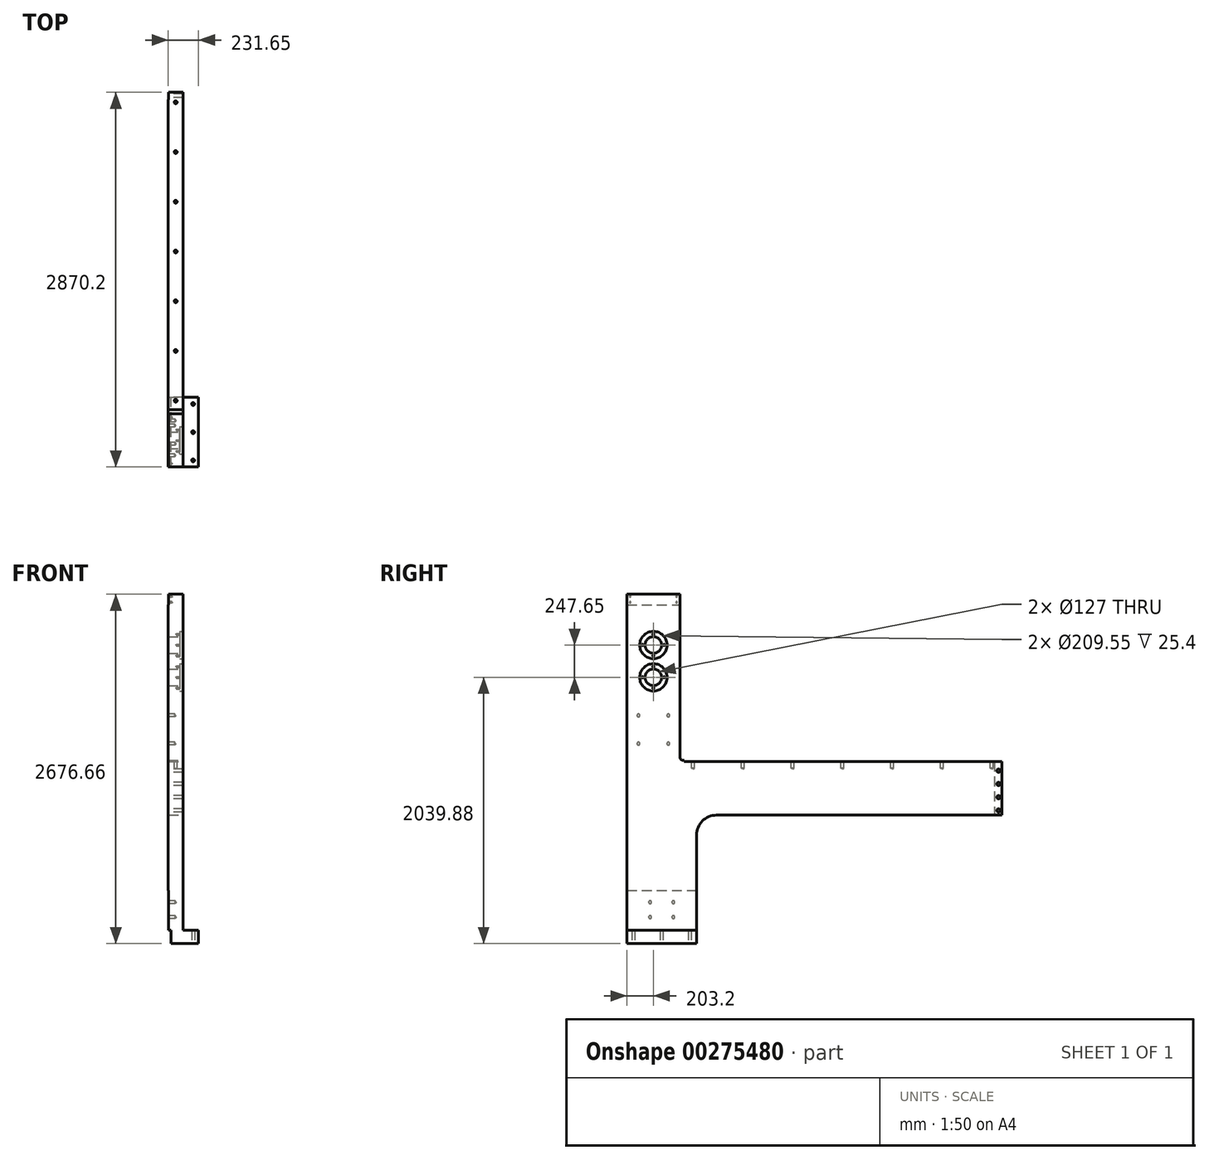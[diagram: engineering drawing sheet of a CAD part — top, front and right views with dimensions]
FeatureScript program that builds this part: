
annotation { "Feature Type Name" : "Feature", "Feature Type Description" : "" }
export const myFeature = defineFeature(function(context is Context, id is Id, definition is map)
    precondition{}
    {
        {
            var Q0;
            Q0=qCreatedBy(makeId("Right.planeOp"),FACE);
            var sketch = newSketch(context, id + "F0", { "sketchPlane" : qUnion([Q0])});
            skLineSegment(sketch, "E0", {"start": v(0, 1338.33) * mm, "end": v(0, -1338.33) * mm});
            skLineSegment(sketch, "E1.bottom", {"start": v(0, 1338.33) * mm, "end": v(406.4, 1338.33) * mm});
            skLineSegment(sketch, "E1.left", {"start": v(0, 1338.33) * mm, "end": v(0, -642.77) * mm});
            skLineSegment(sketch, "E1.right", {"start": v(406.4, 1338.33) * mm, "end": v(406.4, 90.42) * mm});
            skLineSegment(sketch, "E2", {"start": v(0, -1338.33) * mm, "end": v(2674.85, -1338.33) * mm, "construction": true});
            skLineSegment(sketch, "E3.0", {"start": v(0, -1236.73) * mm, "end": v(897.1, -1236.73) * mm, "construction": true});
            skLineSegment(sketch, "E4.bottom", {"start": v(0, -1236.73) * mm, "end": v(533.4, -1236.73) * mm});
            skLineSegment(sketch, "E4.top", {"start": v(406.4, 65.02) * mm, "end": v(438.15, 65.02) * mm});
            skLineSegment(sketch, "E4.left", {"start": v(0, -1236.73) * mm, "end": v(0, 65.02) * mm});
            skLineSegment(sketch, "E4.right", {"start": v(533.4, -1236.73) * mm, "end": v(533.4, -506.48) * mm});
            skLineSegment(sketch, "E5.bottom", {"start": v(431.8, 65.02) * mm, "end": v(438.15, 65.02) * mm});
            skLineSegment(sketch, "E5.top", {"start": v(685.8, -354.08) * mm, "end": v(2870.2, -354.08) * mm});
            skLineSegment(sketch, "E5.left", {"start": v(0, 65.02) * mm, "end": v(0, -354.08) * mm});
            skLineSegment(sketch, "E5.right", {"start": v(2870.2, 57.02) * mm, "end": v(2870.2, -354.08) * mm});
            skPoint(sketch, "E6.visualSharp", {"position": v(533.4, -354.08) * mm});
            skArc(sketch, "E6.filletArc", {"start": v(685.8, -354.08) * mm, "mid": v(578.04, -398.71) * mm, "end": v(533.4, -506.48) * mm});
            skPoint(sketch, "E7.visualSharp", {"position": v(406.4, 65.02) * mm});
            skArc(sketch, "E7.filletArc", {"start": v(406.4, 90.42) * mm, "mid": v(413.84, 72.46) * mm, "end": v(431.8, 65.02) * mm});
            skLineSegment(sketch, "E8.0", {"start": v(0, 701.55) * mm, "end": v(2674.85, 701.55) * mm, "construction": true});
            skLineSegment(sketch, "E9.0", {"start": v(0, 949.2) * mm, "end": v(2674.85, 949.2) * mm, "construction": true});
            skLineSegment(sketch, "E10", {"start": v(203.2, 1338.33) * mm, "end": v(203.2, -548.87) * mm, "construction": true});
            skCircle(sketch, "E11", {"center": v(203.2, 949.2) * mm, "radius": 63.5 * mm});
            skCircle(sketch, "E12", {"center": v(203.2, 701.55) * mm, "radius": 63.5 * mm});
            skLineSegment(sketch, "E13.0", {"start": v(438.15, 1338.33) * mm, "end": v(438.15, 701.55) * mm, "construction": true});
            skLineSegment(sketch, "E14.0", {"start": v(0, 57.02) * mm, "end": v(203.2, 57.02) * mm, "construction": true});
            skLineSegment(sketch, "E15.trimOffspring", {"start": v(438.15, 57.02) * mm, "end": v(2870.2, 57.02) * mm});
            skLineSegment(sketch, "E16.trimOffspring", {"start": v(438.15, 65.02) * mm, "end": v(438.15, 57.02) * mm});
            skSolve(sketch);
        }
        {
            var Q0;
            Q0=qSketchRegion(id+"F0",true);
            extrude(context, id + "F1", {"entities" : qUnion([Q0]), "endBound" : BoundingType.SYMMETRIC, "depth" : 114.3 * mm});
        }
        {
            var Q0;
            Q0=makeQuery(id+"F1.opExtrude","CAP_FACE",FACE,{"disambiguationData":[OSD([sQuery(id+"F0.wireOp",EDGE,"E1.bottom"),sQuery(id+"F0.wireOp",EDGE,"E1.left"),sQuery(id+"F0.wireOp",EDGE,"E1.right"),sQuery(id+"F0.wireOp",EDGE,"E4.bottom"),sQuery(id+"F0.wireOp",EDGE,"E4.left"),sQuery(id+"F0.wireOp",EDGE,"E4.right"),sQuery(id+"F0.wireOp",EDGE,"E5.bottom"),sQuery(id+"F0.wireOp",EDGE,"E5.top"),sQuery(id+"F0.wireOp",EDGE,"E5.left"),sQuery(id+"F0.wireOp",EDGE,"E5.right"),sQuery(id+"F0.wireOp",EDGE,"E6.filletArc"),sQuery(id+"F0.wireOp",EDGE,"E7.filletArc"),sQuery(id+"F0.wireOp",EDGE,"E11"),sQuery(id+"F0.wireOp",EDGE,"E12"),sQuery(id+"F0.wireOp",EDGE,"E15.trimOffspring"),sQuery(id+"F0.wireOp",EDGE,"E16.trimOffspring")])],"isStart":false});
            var sketch = newSketch(context, id + "F2", { "sketchPlane" : qUnion([Q0])});
            skLineSegment(sketch, "E17.bottom", {"start": v(0, 1338.33) * mm, "end": v(406.4, 1338.33) * mm});
            skLineSegment(sketch, "E17.top", {"start": v(0, 1255.78) * mm, "end": v(406.4, 1255.78) * mm});
            skLineSegment(sketch, "E17.left", {"start": v(0, 1338.33) * mm, "end": v(0, 1255.78) * mm});
            skLineSegment(sketch, "E17.right", {"start": v(406.4, 1338.33) * mm, "end": v(406.4, 1255.78) * mm});
            skSolve(sketch);
        }
        {
            var Q0;
            Q0=makeQuery(id+"F2.imprint","IMPRINT",FACE,{"disambiguationData":[TD([[makeQuery(id+"F2.imprint","IMPRINT",EDGE,{"derivedFrom":sQuery(id+"F2.wireOp",EDGE,"E17.bottom")}),-1.0]])]});
            extrude(context, id + "F3", {"entities" : qUnion([Q0]), "operationType" : NewBodyOperationType.REMOVE, "oppositeDirection" : true, "depth" : 3.05 * mm});
        }
        {
            var Q0;
            Q0=makeQuery(id+"F3.boolean.opBoolean","COPY",FACE,{"derivedFrom":makeQuery(id+"F3.opExtrude","CAP_FACE",FACE,{"disambiguationData":[OSD([sQuery(id+"F2.wireOp",EDGE,"E17.bottom"),sQuery(id+"F2.wireOp",EDGE,"E17.top"),sQuery(id+"F2.wireOp",EDGE,"E17.left"),sQuery(id+"F2.wireOp",EDGE,"E17.right")])],"isStart":false})});
            var sketch = newSketch(context, id + "F4", { "sketchPlane" : qUnion([Q0])});
            skLineSegment(sketch, "E18", {"start": v(203.2, 1338.33) * mm, "end": v(203.2, 1255.78) * mm, "construction": true});
            skCircle(sketch, "E19.0", {"center": v(203.2, 949.2) * mm, "radius": 63.5 * mm, "construction": true});
            skLineSegment(sketch, "E20", {"start": v(203.2, 949.2) * mm, "end": v(580.51, 949.2) * mm, "construction": true});
            skLineSegment(sketch, "E21.0", {"start": v(25.4, 1276.22) * mm, "end": v(580.51, 1276.22) * mm, "construction": true});
            skLineSegment(sketch, "E22.0", {"start": v(25.4, 1320.67) * mm, "end": v(580.51, 1320.67) * mm, "construction": true});
            skLineSegment(sketch, "E23.0", {"start": v(25.4, 1338.33) * mm, "end": v(25.4, 1255.78) * mm, "construction": true});
            skPoint(sketch, "E24", {"position": v(25.4, 1320.67) * mm});
            skPoint(sketch, "E25", {"position": v(25.4, 1276.22) * mm});
            skPoint(sketch, "E26.MirrorP", {"position": v(381, 1320.67) * mm});
            skPoint(sketch, "E27.MirrorP", {"position": v(381, 1276.22) * mm});
            skSolve(sketch);
        }
        {
            var Q0;
            Q0=sQuery(id+"F4.wireOp",VERTEX,"E24");
            var Q1;
            Q1=sQuery(id+"F4.wireOp",VERTEX,"E25");
            var Q2;
            Q2=sQuery(id+"F4.wireOp",VERTEX,"E26.MirrorP");
            var Q3;
            Q3=sQuery(id+"F4.wireOp",VERTEX,"E27.MirrorP");
            var Q4;
            Q4=makeQuery(id+"F1.opExtrude","SWEPT_BODY",BODY,{"disambiguationData":[OSD([sQuery(id+"F0.wireOp",EDGE,"E1.bottom"),sQuery(id+"F0.wireOp",EDGE,"E1.left"),sQuery(id+"F0.wireOp",EDGE,"E1.right"),sQuery(id+"F0.wireOp",EDGE,"E4.bottom"),sQuery(id+"F0.wireOp",EDGE,"E4.left"),sQuery(id+"F0.wireOp",EDGE,"E4.right"),sQuery(id+"F0.wireOp",EDGE,"E5.bottom"),sQuery(id+"F0.wireOp",EDGE,"E5.top"),sQuery(id+"F0.wireOp",EDGE,"E5.left"),sQuery(id+"F0.wireOp",EDGE,"E5.right"),sQuery(id+"F0.wireOp",EDGE,"E6.filletArc"),sQuery(id+"F0.wireOp",EDGE,"E7.filletArc"),sQuery(id+"F0.wireOp",EDGE,"E11"),sQuery(id+"F0.wireOp",EDGE,"E12"),sQuery(id+"F0.wireOp",EDGE,"E15.trimOffspring"),sQuery(id+"F0.wireOp",EDGE,"E16.trimOffspring")])]});
            hole(context, id + "F5", {"style" : HoleStyle.SIMPLE, "endStyle" : HoleEndStyle.BLIND, "standardTappedOrClearance" : lookupTablePath({ "standard" : "ANSI", "engagement" : "75%", "pitch" : "13 tpi", "size" : "1/2", "type" : "Tapped" }), "standardBlindInLast" : lookupTablePath({ "standard" : "ANSI", "engagement" : "75%", "pitch" : "13 tpi", "size" : "1/2", "type" : "Tapped" }), "holeDiameter" : 10.72 * mm, "showTappedDepth" : true, "holeDepth" : 25.4 * mm, "tappedDepth" : 19.54 * mm, "tapClearance" : 3, "startFromSketch" : true, "locations" : qUnion([Q0, Q1, Q2, Q3]), "scope" : qUnion([Q4]), "majorDiameter" : 12.7 * mm});
        }
        {
            var Q0;
            Q0=makeQuery(id+"F1.opExtrude","CAP_FACE",FACE,{"disambiguationData":[OSD([sQuery(id+"F0.wireOp",EDGE,"E1.bottom"),sQuery(id+"F0.wireOp",EDGE,"E1.left"),sQuery(id+"F0.wireOp",EDGE,"E1.right"),sQuery(id+"F0.wireOp",EDGE,"E4.bottom"),sQuery(id+"F0.wireOp",EDGE,"E4.left"),sQuery(id+"F0.wireOp",EDGE,"E4.right"),sQuery(id+"F0.wireOp",EDGE,"E5.bottom"),sQuery(id+"F0.wireOp",EDGE,"E5.top"),sQuery(id+"F0.wireOp",EDGE,"E5.left"),sQuery(id+"F0.wireOp",EDGE,"E5.right"),sQuery(id+"F0.wireOp",EDGE,"E6.filletArc"),sQuery(id+"F0.wireOp",EDGE,"E7.filletArc"),sQuery(id+"F0.wireOp",EDGE,"E11"),sQuery(id+"F0.wireOp",EDGE,"E12"),sQuery(id+"F0.wireOp",EDGE,"E15.trimOffspring"),sQuery(id+"F0.wireOp",EDGE,"E16.trimOffspring")])],"isStart":true});
            var sketch = newSketch(context, id + "F6", { "sketchPlane" : qUnion([Q0])});
            skCircle(sketch, "E28.0", {"center": v(-203.2, 949.2) * mm, "radius": 63.5 * mm, "construction": true});
            skCircle(sketch, "E29.0", {"center": v(-203.2, 701.55) * mm, "radius": 63.5 * mm, "construction": true});
            skCircle(sketch, "E30", {"center": v(-203.2, 949.2) * mm, "radius": 104.78 * mm});
            skCircle(sketch, "E31", {"center": v(-203.2, 701.55) * mm, "radius": 104.78 * mm});
            skSolve(sketch);
        }
        {
            var Q0;
            Q0=qSketchRegion(id+"F6",true);
            extrude(context, id + "F7", {"entities" : qUnion([Q0]), "operationType" : NewBodyOperationType.REMOVE, "oppositeDirection" : true, "depth" : 25.4 * mm});
        }
        {
            var Q0;
            Q0=makeQuery(id+"F7.boolean.opBoolean","COPY",FACE,{"derivedFrom":makeQuery(id+"F7.opExtrude","CAP_FACE",FACE,{"disambiguationData":[OSD([sQuery(id+"F6.wireOp",EDGE,"E30")])],"isStart":false})});
            var sketch = newSketch(context, id + "F8", { "sketchPlane" : qUnion([Q0])});
            skCircle(sketch, "E32.0", {"center": v(-203.2, 949.2) * mm, "radius": 63.5 * mm, "construction": true});
            skCircle(sketch, "E33.0", {"center": v(-203.2, 701.55) * mm, "radius": 63.5 * mm, "construction": true});
            skCircle(sketch, "E34", {"center": v(-203.2, 949.2) * mm, "radius": 82.55 * mm, "construction": true});
            skLineSegment(sketch, "E35", {"start": v(-203.2, 949.2) * mm, "end": v(-203.2, 1031.75) * mm, "construction": true});
            skPoint(sketch, "E36", {"position": v(-203.2, 1031.75) * mm});
            skPoint(sketch, "E37.1.0", {"position": v(-285.75, 949.2) * mm});
            skPoint(sketch, "E37.2.0", {"position": v(-203.2, 866.65) * mm});
            skPoint(sketch, "E37.3.0", {"position": v(-120.65, 949.2) * mm});
            skLineSegment(sketch, "E38.0.1.0", {"start": v(-203.2, 701.55) * mm, "end": v(-203.2, 784.1) * mm, "construction": true});
            skCircle(sketch, "E38.0.1.1", {"center": v(-203.2, 701.55) * mm, "radius": 82.55 * mm, "construction": true});
            skPoint(sketch, "E38.0.1.2", {"position": v(-203.2, 784.1) * mm});
            skPoint(sketch, "E38.0.1.3", {"position": v(-285.75, 701.55) * mm});
            skPoint(sketch, "E38.0.1.4", {"position": v(-203.2, 619) * mm});
            skPoint(sketch, "E38.0.1.5", {"position": v(-120.65, 701.55) * mm});
            skLineSegment(sketch, "E38.direction1", {"start": v(-203.2, 866.65) * mm, "end": v(-177.8, 866.65) * mm, "construction": true});
            skLineSegment(sketch, "E38.direction2", {"start": v(-203.2, 866.65) * mm, "end": v(-203.2, 619) * mm, "construction": true});
            skSolve(sketch);
        }
        {
            var Q0;
            Q0=sQuery(id+"F8.wireOp",VERTEX,"E36");
            var Q1;
            Q1=sQuery(id+"F8.wireOp",VERTEX,"E37.3.0");
            var Q2;
            Q2=sQuery(id+"F8.wireOp",VERTEX,"E37.2.0");
            var Q3;
            Q3=sQuery(id+"F8.wireOp",VERTEX,"E37.1.0");
            var Q4;
            Q4=sQuery(id+"F8.wireOp",VERTEX,"E38.0.1.2");
            var Q5;
            Q5=sQuery(id+"F8.wireOp",VERTEX,"E38.0.1.5");
            var Q6;
            Q6=sQuery(id+"F8.wireOp",VERTEX,"E38.0.1.4");
            var Q7;
            Q7=sQuery(id+"F8.wireOp",VERTEX,"E38.0.1.3");
            var Q8;
            Q8=makeQuery(id+"F1.opExtrude","SWEPT_BODY",BODY,{"disambiguationData":[OSD([sQuery(id+"F0.wireOp",EDGE,"E1.bottom"),sQuery(id+"F0.wireOp",EDGE,"E1.left"),sQuery(id+"F0.wireOp",EDGE,"E1.right"),sQuery(id+"F0.wireOp",EDGE,"E4.bottom"),sQuery(id+"F0.wireOp",EDGE,"E4.left"),sQuery(id+"F0.wireOp",EDGE,"E4.right"),sQuery(id+"F0.wireOp",EDGE,"E5.bottom"),sQuery(id+"F0.wireOp",EDGE,"E5.top"),sQuery(id+"F0.wireOp",EDGE,"E5.left"),sQuery(id+"F0.wireOp",EDGE,"E5.right"),sQuery(id+"F0.wireOp",EDGE,"E6.filletArc"),sQuery(id+"F0.wireOp",EDGE,"E7.filletArc"),sQuery(id+"F0.wireOp",EDGE,"E11"),sQuery(id+"F0.wireOp",EDGE,"E12"),sQuery(id+"F0.wireOp",EDGE,"E15.trimOffspring"),sQuery(id+"F0.wireOp",EDGE,"E16.trimOffspring")])]});
            hole(context, id + "F9", {"style" : HoleStyle.SIMPLE, "endStyle" : HoleEndStyle.BLIND, "standardTappedOrClearance" : lookupTablePath({ "standard" : "ANSI", "engagement" : "75%", "pitch" : "13 tpi", "size" : "1/2", "type" : "Tapped" }), "standardBlindInLast" : lookupTablePath({ "standard" : "ANSI", "engagement" : "75%", "pitch" : "13 tpi", "size" : "1/2", "type" : "Tapped" }), "holeDiameter" : 10.72 * mm, "showTappedDepth" : true, "holeDepth" : 25.4 * mm, "tappedDepth" : 19.54 * mm, "tapClearance" : 3, "startFromSketch" : true, "locations" : qUnion([Q0, Q1, Q2, Q3, Q4, Q5, Q6, Q7]), "scope" : qUnion([Q8]), "majorDiameter" : 12.7 * mm});
        }
        {
            var Q0;
            Q0=makeQuery(id+"F1.opExtrude","CAP_FACE",FACE,{"disambiguationData":[OSD([sQuery(id+"F0.wireOp",EDGE,"E1.bottom"),sQuery(id+"F0.wireOp",EDGE,"E1.left"),sQuery(id+"F0.wireOp",EDGE,"E1.right"),sQuery(id+"F0.wireOp",EDGE,"E4.bottom"),sQuery(id+"F0.wireOp",EDGE,"E4.left"),sQuery(id+"F0.wireOp",EDGE,"E4.right"),sQuery(id+"F0.wireOp",EDGE,"E5.bottom"),sQuery(id+"F0.wireOp",EDGE,"E5.top"),sQuery(id+"F0.wireOp",EDGE,"E5.left"),sQuery(id+"F0.wireOp",EDGE,"E5.right"),sQuery(id+"F0.wireOp",EDGE,"E6.filletArc"),sQuery(id+"F0.wireOp",EDGE,"E7.filletArc"),sQuery(id+"F0.wireOp",EDGE,"E11"),sQuery(id+"F0.wireOp",EDGE,"E12"),sQuery(id+"F0.wireOp",EDGE,"E15.trimOffspring"),sQuery(id+"F0.wireOp",EDGE,"E16.trimOffspring")])],"isStart":false});
            var sketch = newSketch(context, id + "F10", { "sketchPlane" : qUnion([Q0])});
            skCircle(sketch, "E39.0", {"center": v(203.2, 701.55) * mm, "radius": 63.5 * mm, "construction": true});
            skLineSegment(sketch, "E40", {"start": v(203.2, 701.55) * mm, "end": v(203.2, -117.25) * mm, "construction": true});
            skLineSegment(sketch, "E41", {"start": v(203.2, 701.55) * mm, "end": v(767.73, 701.55) * mm, "construction": true});
            skLineSegment(sketch, "E42.0", {"start": v(203.2, 409.45) * mm, "end": v(767.73, 409.45) * mm, "construction": true});
            skLineSegment(sketch, "E43.0", {"start": v(203.2, 193.55) * mm, "end": v(767.73, 193.55) * mm, "construction": true});
            skLineSegment(sketch, "E44.0", {"start": v(317.5, 701.55) * mm, "end": v(317.5, -117.25) * mm, "construction": true});
            skPoint(sketch, "E45", {"position": v(317.5, 409.45) * mm});
            skPoint(sketch, "E46", {"position": v(317.5, 193.55) * mm});
            skPoint(sketch, "E47.MirrorP", {"position": v(88.9, 409.45) * mm});
            skPoint(sketch, "E48.MirrorP", {"position": v(88.9, 193.55) * mm});
            skSolve(sketch);
        }
        {
            var Q0;
            Q0=sQuery(id+"F10.wireOp",VERTEX,"E47.MirrorP");
            var Q1;
            Q1=sQuery(id+"F10.wireOp",VERTEX,"E45");
            var Q2;
            Q2=sQuery(id+"F10.wireOp",VERTEX,"E48.MirrorP");
            var Q3;
            Q3=sQuery(id+"F10.wireOp",VERTEX,"E46");
            var Q4;
            Q4=makeQuery(id+"F1.opExtrude","SWEPT_BODY",BODY,{"disambiguationData":[OSD([sQuery(id+"F0.wireOp",EDGE,"E1.bottom"),sQuery(id+"F0.wireOp",EDGE,"E1.left"),sQuery(id+"F0.wireOp",EDGE,"E1.right"),sQuery(id+"F0.wireOp",EDGE,"E4.bottom"),sQuery(id+"F0.wireOp",EDGE,"E4.left"),sQuery(id+"F0.wireOp",EDGE,"E4.right"),sQuery(id+"F0.wireOp",EDGE,"E5.bottom"),sQuery(id+"F0.wireOp",EDGE,"E5.top"),sQuery(id+"F0.wireOp",EDGE,"E5.left"),sQuery(id+"F0.wireOp",EDGE,"E5.right"),sQuery(id+"F0.wireOp",EDGE,"E6.filletArc"),sQuery(id+"F0.wireOp",EDGE,"E7.filletArc"),sQuery(id+"F0.wireOp",EDGE,"E11"),sQuery(id+"F0.wireOp",EDGE,"E12"),sQuery(id+"F0.wireOp",EDGE,"E15.trimOffspring"),sQuery(id+"F0.wireOp",EDGE,"E16.trimOffspring")])]});
            hole(context, id + "F11", {"style" : HoleStyle.SIMPLE, "endStyle" : HoleEndStyle.BLIND, "standardTappedOrClearance" : lookupTablePath({ "standard" : "ANSI", "engagement" : "75%", "pitch" : "8 tpi", "size" : "1", "type" : "Tapped" }), "standardBlindInLast" : lookupTablePath({ "standard" : "ANSI", "engagement" : "75%", "pitch" : "8 tpi", "size" : "1", "type" : "Tapped" }), "holeDiameter" : 22.22 * mm, "showTappedDepth" : true, "holeDepth" : 50.8 * mm, "tappedDepth" : 41.27 * mm, "tapClearance" : 3, "startFromSketch" : true, "locations" : qUnion([Q0, Q1, Q2, Q3]), "scope" : qUnion([Q4]), "majorDiameter" : 25.4 * mm});
        }
        {
            var Q0;
            Q0=makeQuery(id+"F1.opExtrude","CAP_FACE",FACE,{"disambiguationData":[OSD([sQuery(id+"F0.wireOp",EDGE,"E1.bottom"),sQuery(id+"F0.wireOp",EDGE,"E1.left"),sQuery(id+"F0.wireOp",EDGE,"E1.right"),sQuery(id+"F0.wireOp",EDGE,"E4.bottom"),sQuery(id+"F0.wireOp",EDGE,"E4.left"),sQuery(id+"F0.wireOp",EDGE,"E4.right"),sQuery(id+"F0.wireOp",EDGE,"E5.bottom"),sQuery(id+"F0.wireOp",EDGE,"E5.top"),sQuery(id+"F0.wireOp",EDGE,"E5.left"),sQuery(id+"F0.wireOp",EDGE,"E5.right"),sQuery(id+"F0.wireOp",EDGE,"E6.filletArc"),sQuery(id+"F0.wireOp",EDGE,"E7.filletArc"),sQuery(id+"F0.wireOp",EDGE,"E11"),sQuery(id+"F0.wireOp",EDGE,"E12"),sQuery(id+"F0.wireOp",EDGE,"E15.trimOffspring"),sQuery(id+"F0.wireOp",EDGE,"E16.trimOffspring")])],"isStart":false});
            var sketch = newSketch(context, id + "F12", { "sketchPlane" : qUnion([Q0])});
            skLineSegment(sketch, "E49.bottom", {"start": v(2870.2, 57.02) * mm, "end": v(2813.05, 57.02) * mm});
            skLineSegment(sketch, "E49.top", {"start": v(2870.2, -354.08) * mm, "end": v(2813.05, -354.08) * mm});
            skLineSegment(sketch, "E49.left", {"start": v(2870.2, 57.02) * mm, "end": v(2870.2, -354.08) * mm});
            skLineSegment(sketch, "E49.right", {"start": v(2813.05, 57.02) * mm, "end": v(2813.05, -354.08) * mm});
            skSolve(sketch);
        }
        {
            var Q0;
            Q0=qSketchRegion(id+"F12",true);
            extrude(context, id + "F13", {"entities" : qUnion([Q0]), "operationType" : NewBodyOperationType.REMOVE, "oppositeDirection" : true, "depth" : 3.17 * mm});
        }
        {
            var Q0;
            Q0=makeQuery(id+"F13.boolean.opBoolean","COPY",FACE,{"derivedFrom":makeQuery(id+"F13.opExtrude","CAP_FACE",FACE,{"disambiguationData":[OSD([sQuery(id+"F12.wireOp",EDGE,"E49.bottom"),sQuery(id+"F12.wireOp",EDGE,"E49.top"),sQuery(id+"F12.wireOp",EDGE,"E49.left"),sQuery(id+"F12.wireOp",EDGE,"E49.right")])],"isStart":false})});
            var sketch = newSketch(context, id + "F14", { "sketchPlane" : qUnion([Q0])});
            skLineSegment(sketch, "E50.0", {"start": v(2813.05, 57.02) * mm, "end": v(2870.2, 57.02) * mm, "construction": true});
            skCircle(sketch, "E51.0", {"center": v(203.2, 701.55) * mm, "radius": 63.5 * mm, "construction": true});
            skLineSegment(sketch, "E52", {"start": v(203.2, 701.55) * mm, "end": v(203.2, -538.92) * mm, "construction": true});
            skLineSegment(sketch, "E53.0", {"start": v(2844.8, 701.55) * mm, "end": v(2844.8, -538.92) * mm, "construction": true});
            skLineSegment(sketch, "E54.0", {"start": v(2813.05, -12.83) * mm, "end": v(2870.2, -12.83) * mm, "construction": true});
            skPoint(sketch, "E55", {"position": v(2844.8, -12.83) * mm});
            skPoint(sketch, "E56.0.1.0", {"position": v(2844.8, -114.43) * mm});
            skPoint(sketch, "E56.0.2.0", {"position": v(2844.8, -216.03) * mm});
            skPoint(sketch, "E56.0.3.0", {"position": v(2844.8, -317.63) * mm});
            skLineSegment(sketch, "E56.direction1", {"start": v(2844.8, -12.83) * mm, "end": v(2870.2, -12.83) * mm, "construction": true});
            skLineSegment(sketch, "E56.direction2", {"start": v(2844.8, -12.83) * mm, "end": v(2844.8, -114.43) * mm, "construction": true});
            skSolve(sketch);
        }
        {
            var Q0;
            Q0=sQuery(id+"F14.wireOp",VERTEX,"E55");
            var Q1;
            Q1=sQuery(id+"F14.wireOp",VERTEX,"E56.0.1.0");
            var Q2;
            Q2=sQuery(id+"F14.wireOp",VERTEX,"E56.0.2.0");
            var Q3;
            Q3=sQuery(id+"F14.wireOp",VERTEX,"E56.0.3.0");
            var Q4;
            Q4=makeQuery(id+"F1.opExtrude","SWEPT_BODY",BODY,{"disambiguationData":[OSD([sQuery(id+"F0.wireOp",EDGE,"E1.bottom"),sQuery(id+"F0.wireOp",EDGE,"E1.left"),sQuery(id+"F0.wireOp",EDGE,"E1.right"),sQuery(id+"F0.wireOp",EDGE,"E4.bottom"),sQuery(id+"F0.wireOp",EDGE,"E4.left"),sQuery(id+"F0.wireOp",EDGE,"E4.right"),sQuery(id+"F0.wireOp",EDGE,"E5.bottom"),sQuery(id+"F0.wireOp",EDGE,"E5.top"),sQuery(id+"F0.wireOp",EDGE,"E5.left"),sQuery(id+"F0.wireOp",EDGE,"E5.right"),sQuery(id+"F0.wireOp",EDGE,"E6.filletArc"),sQuery(id+"F0.wireOp",EDGE,"E7.filletArc"),sQuery(id+"F0.wireOp",EDGE,"E11"),sQuery(id+"F0.wireOp",EDGE,"E12"),sQuery(id+"F0.wireOp",EDGE,"E15.trimOffspring"),sQuery(id+"F0.wireOp",EDGE,"E16.trimOffspring")])]});
            hole(context, id + "F15", {"style" : HoleStyle.SIMPLE, "endStyle" : HoleEndStyle.THROUGH, "holeDiameter" : 26.92 * mm, "tappedDepth" : 41.27 * mm, "tapClearance" : 3, "startFromSketch" : true, "locations" : qUnion([Q0, Q1, Q2, Q3]), "scope" : qUnion([Q4])});
        }
        {
            var Q0;
            Q0=makeQuery(id+"F1.opExtrude","SWEPT_FACE",FACE,{"disambiguationData":[OSD([sQuery(id+"F0.wireOp",EDGE,"E15.trimOffspring")])]});
            var sketch = newSketch(context, id + "F16", { "sketchPlane" : qUnion([Q0])});
            skLineSegment(sketch, "E57", {"start": v(0, -474.51) * mm, "end": v(0, 3159.2) * mm, "construction": true});
            skLineSegment(sketch, "E58.0", {"start": v(-31.75, 98.43) * mm, "end": v(-31.75, 307.98) * mm, "construction": true});
            skLineSegment(sketch, "E59", {"start": v(-31.75, 203.2) * mm, "end": v(158.49, 203.2) * mm, "construction": true});
            skLineSegment(sketch, "E60.0", {"start": v(-31.75, 508) * mm, "end": v(158.49, 508) * mm, "construction": true});
            skPoint(sketch, "E61", {"position": v(0, 508) * mm});
            skPoint(sketch, "E62.0.1.0", {"position": v(0, 889) * mm});
            skPoint(sketch, "E62.0.2.0", {"position": v(0, 1270) * mm});
            skPoint(sketch, "E62.0.3.0", {"position": v(0, 1651) * mm});
            skPoint(sketch, "E62.0.4.0", {"position": v(0, 2032) * mm});
            skPoint(sketch, "E62.0.5.0", {"position": v(0, 2413) * mm});
            skPoint(sketch, "E62.0.6.0", {"position": v(0, 2794) * mm});
            skLineSegment(sketch, "E62.direction1", {"start": v(0, 508) * mm, "end": v(25.4, 508) * mm, "construction": true});
            skLineSegment(sketch, "E62.direction2", {"start": v(0, 508) * mm, "end": v(0, 889) * mm, "construction": true});
            skSolve(sketch);
        }
        {
            var Q0;
            Q0=sQuery(id+"F16.wireOp",VERTEX,"E61");
            var Q1;
            Q1=sQuery(id+"F16.wireOp",VERTEX,"E62.0.1.0");
            var Q2;
            Q2=sQuery(id+"F16.wireOp",VERTEX,"E62.0.2.0");
            var Q3;
            Q3=sQuery(id+"F16.wireOp",VERTEX,"E62.0.3.0");
            var Q4;
            Q4=sQuery(id+"F16.wireOp",VERTEX,"E62.0.4.0");
            var Q5;
            Q5=sQuery(id+"F16.wireOp",VERTEX,"E62.0.5.0");
            var Q6;
            Q6=sQuery(id+"F16.wireOp",VERTEX,"E62.0.6.0");
            var Q7;
            Q7=makeQuery(id+"F1.opExtrude","SWEPT_BODY",BODY,{"disambiguationData":[OSD([sQuery(id+"F0.wireOp",EDGE,"E1.bottom"),sQuery(id+"F0.wireOp",EDGE,"E1.left"),sQuery(id+"F0.wireOp",EDGE,"E1.right"),sQuery(id+"F0.wireOp",EDGE,"E4.bottom"),sQuery(id+"F0.wireOp",EDGE,"E4.left"),sQuery(id+"F0.wireOp",EDGE,"E4.right"),sQuery(id+"F0.wireOp",EDGE,"E5.bottom"),sQuery(id+"F0.wireOp",EDGE,"E5.top"),sQuery(id+"F0.wireOp",EDGE,"E5.left"),sQuery(id+"F0.wireOp",EDGE,"E5.right"),sQuery(id+"F0.wireOp",EDGE,"E6.filletArc"),sQuery(id+"F0.wireOp",EDGE,"E7.filletArc"),sQuery(id+"F0.wireOp",EDGE,"E11"),sQuery(id+"F0.wireOp",EDGE,"E12"),sQuery(id+"F0.wireOp",EDGE,"E15.trimOffspring"),sQuery(id+"F0.wireOp",EDGE,"E16.trimOffspring")])]});
            hole(context, id + "F17", {"style" : HoleStyle.SIMPLE, "endStyle" : HoleEndStyle.BLIND, "standardTappedOrClearance" : lookupTablePath({ "standard" : "ANSI", "engagement" : "75%", "pitch" : "8 tpi", "size" : "1", "type" : "Tapped" }), "standardBlindInLast" : lookupTablePath({ "standard" : "ANSI", "engagement" : "75%", "pitch" : "8 tpi", "size" : "1", "type" : "Tapped" }), "holeDiameter" : 22.22 * mm, "showTappedDepth" : true, "holeDepth" : 50.8 * mm, "tappedDepth" : 41.27 * mm, "tapClearance" : 3, "startFromSketch" : true, "locations" : qUnion([Q0, Q1, Q2, Q3, Q4, Q5, Q6]), "scope" : qUnion([Q7]), "majorDiameter" : 25.4 * mm});
        }
        {
            var Q0;
            Q0=makeQuery(id+"F1.opExtrude","CAP_FACE",FACE,{"disambiguationData":[OSD([sQuery(id+"F0.wireOp",EDGE,"E1.bottom"),sQuery(id+"F0.wireOp",EDGE,"E1.left"),sQuery(id+"F0.wireOp",EDGE,"E1.right"),sQuery(id+"F0.wireOp",EDGE,"E4.bottom"),sQuery(id+"F0.wireOp",EDGE,"E4.left"),sQuery(id+"F0.wireOp",EDGE,"E4.right"),sQuery(id+"F0.wireOp",EDGE,"E5.bottom"),sQuery(id+"F0.wireOp",EDGE,"E5.top"),sQuery(id+"F0.wireOp",EDGE,"E5.left"),sQuery(id+"F0.wireOp",EDGE,"E5.right"),sQuery(id+"F0.wireOp",EDGE,"E6.filletArc"),sQuery(id+"F0.wireOp",EDGE,"E7.filletArc"),sQuery(id+"F0.wireOp",EDGE,"E11"),sQuery(id+"F0.wireOp",EDGE,"E12"),sQuery(id+"F0.wireOp",EDGE,"E15.trimOffspring"),sQuery(id+"F0.wireOp",EDGE,"E16.trimOffspring")])],"isStart":false});
            var sketch = newSketch(context, id + "F18", { "sketchPlane" : qUnion([Q0])});
            skLineSegment(sketch, "E63.bottom", {"start": v(0, -1236.73) * mm, "end": v(533.4, -1236.73) * mm});
            skLineSegment(sketch, "E63.top", {"start": v(0, -931.93) * mm, "end": v(533.4, -931.93) * mm});
            skLineSegment(sketch, "E63.left", {"start": v(0, -1236.73) * mm, "end": v(0, -931.93) * mm});
            skLineSegment(sketch, "E63.right", {"start": v(533.4, -1236.73) * mm, "end": v(533.4, -931.93) * mm});
            skSolve(sketch);
        }
        {
            var Q0;
            Q0=makeQuery(id+"F18.imprint","IMPRINT",FACE,{"disambiguationData":[TD([[makeQuery(id+"F18.imprint","IMPRINT",EDGE,{"derivedFrom":sQuery(id+"F18.wireOp",EDGE,"E63.bottom")}),1.0]])]});
            extrude(context, id + "F19", {"entities" : qUnion([Q0]), "operationType" : NewBodyOperationType.REMOVE, "oppositeDirection" : true, "depth" : 3.05 * mm});
        }
        {
            var Q0;
            Q0=makeQuery(id+"F19.boolean.opBoolean","COPY",FACE,{"derivedFrom":makeQuery(id+"F19.opExtrude","CAP_FACE",FACE,{"disambiguationData":[OSD([sQuery(id+"F18.wireOp",EDGE,"E63.bottom"),sQuery(id+"F18.wireOp",EDGE,"E63.top"),sQuery(id+"F18.wireOp",EDGE,"E63.left"),sQuery(id+"F18.wireOp",EDGE,"E63.right")])],"isStart":false})});
            var sketch = newSketch(context, id + "F20", { "sketchPlane" : qUnion([Q0])});
            skLineSegment(sketch, "E64.0", {"start": v(0, -1236.73) * mm, "end": v(533.4, -1236.73) * mm, "construction": true});
            skLineSegment(sketch, "E65", {"start": v(266.7, -1236.73) * mm, "end": v(266.7, -931.93) * mm, "construction": true});
            skLineSegment(sketch, "E66.0", {"start": v(0, -1135.13) * mm, "end": v(533.4, -1135.13) * mm, "construction": true});
            skLineSegment(sketch, "E67.0", {"start": v(0, -1020.83) * mm, "end": v(533.4, -1020.83) * mm, "construction": true});
            skLineSegment(sketch, "E68.0", {"start": v(177.8, -1236.73) * mm, "end": v(177.8, -931.93) * mm, "construction": true});
            skPoint(sketch, "E69", {"position": v(177.8, -1020.83) * mm});
            skPoint(sketch, "E70", {"position": v(177.8, -1135.13) * mm});
            skPoint(sketch, "E71.MirrorP", {"position": v(355.6, -1020.83) * mm});
            skPoint(sketch, "E72.MirrorP", {"position": v(355.6, -1135.13) * mm});
            skSolve(sketch);
        }
        {
            var Q0;
            Q0=sQuery(id+"F20.wireOp",VERTEX,"E69");
            var Q1;
            Q1=sQuery(id+"F20.wireOp",VERTEX,"E71.MirrorP");
            var Q2;
            Q2=sQuery(id+"F20.wireOp",VERTEX,"E72.MirrorP");
            var Q3;
            Q3=sQuery(id+"F20.wireOp",VERTEX,"E70");
            var Q4;
            Q4=makeQuery(id+"F1.opExtrude","SWEPT_BODY",BODY,{"disambiguationData":[OSD([sQuery(id+"F0.wireOp",EDGE,"E1.bottom"),sQuery(id+"F0.wireOp",EDGE,"E1.left"),sQuery(id+"F0.wireOp",EDGE,"E1.right"),sQuery(id+"F0.wireOp",EDGE,"E4.bottom"),sQuery(id+"F0.wireOp",EDGE,"E4.left"),sQuery(id+"F0.wireOp",EDGE,"E4.right"),sQuery(id+"F0.wireOp",EDGE,"E5.bottom"),sQuery(id+"F0.wireOp",EDGE,"E5.top"),sQuery(id+"F0.wireOp",EDGE,"E5.left"),sQuery(id+"F0.wireOp",EDGE,"E5.right"),sQuery(id+"F0.wireOp",EDGE,"E6.filletArc"),sQuery(id+"F0.wireOp",EDGE,"E7.filletArc"),sQuery(id+"F0.wireOp",EDGE,"E11"),sQuery(id+"F0.wireOp",EDGE,"E12"),sQuery(id+"F0.wireOp",EDGE,"E15.trimOffspring"),sQuery(id+"F0.wireOp",EDGE,"E16.trimOffspring")])]});
            hole(context, id + "F21", {"style" : HoleStyle.SIMPLE, "endStyle" : HoleEndStyle.BLIND, "standardTappedOrClearance" : lookupTablePath({ "standard" : "ANSI", "engagement" : "75%", "pitch" : "8 tpi", "size" : "1", "type" : "Tapped" }), "standardBlindInLast" : lookupTablePath({ "standard" : "ANSI", "engagement" : "75%", "pitch" : "8 tpi", "size" : "1", "type" : "Tapped" }), "holeDiameter" : 22.22 * mm, "showTappedDepth" : true, "holeDepth" : 50.8 * mm, "tappedDepth" : 41.27 * mm, "tapClearance" : 3, "startFromSketch" : true, "locations" : qUnion([Q0, Q1, Q2, Q3]), "scope" : qUnion([Q4]), "majorDiameter" : 25.4 * mm});
        }
        {
            var Q0;
            Q0=makeQuery(id+"F19.boolean.opBoolean","COPY",FACE,{"derivedFrom":makeQuery(id+"F19.opExtrude","CAP_FACE",FACE,{"disambiguationData":[OSD([sQuery(id+"F18.wireOp",EDGE,"E63.bottom"),sQuery(id+"F18.wireOp",EDGE,"E63.top"),sQuery(id+"F18.wireOp",EDGE,"E63.left"),sQuery(id+"F18.wireOp",EDGE,"E63.right")])],"isStart":false})});
            cPlane(context, id + "F22", {"entities" : qUnion([Q0]), "cplaneType" : CPlaneType.OFFSET, "offset" : 19.05 * mm, "oppositeDirection" : true, "width" : 152.4 * mm, "height" : 152.4 * mm});
        }
        {
            var Q0;
            Q0=qCreatedBy(id+"F22.planeOp",FACE);
            var sketch = newSketch(context, id + "F23", { "sketchPlane" : qUnion([Q0])});
            skLineSegment(sketch, "E73.0", {"start": v(0, -1236.73) * mm, "end": v(533.4, -1236.73) * mm});
            skLineSegment(sketch, "E74.top", {"start": v(0, -1338.33) * mm, "end": v(533.4, -1338.33) * mm});
            skLineSegment(sketch, "E74.left", {"start": v(0, -1236.73) * mm, "end": v(0, -1338.33) * mm});
            skLineSegment(sketch, "E74.right", {"start": v(533.4, -1236.73) * mm, "end": v(533.4, -1338.33) * mm});
            skSolve(sketch);
        }
        {
            var Q0;
            Q0=makeQuery(id+"F23.imprint","IMPRINT",FACE,{"disambiguationData":[TD([[makeQuery(id+"F23.imprint","IMPRINT",EDGE,{"derivedFrom":sQuery(id+"F23.wireOp",EDGE,"E73.0")}),-1.0]])]});
            extrude(context, id + "F24", {"entities" : qUnion([Q0]), "operationType" : NewBodyOperationType.ADD, "oppositeDirection" : true, "depth" : 209.55 * mm});
        }
        {
            var Q0;
            Q0=makeQuery(id+"F24.opExtrude","SWEPT_FACE",FACE,{"disambiguationData":[OSD([sQuery(id+"F23.wireOp",EDGE,"E74.top")])]});
            var sketch = newSketch(context, id + "F25", { "sketchPlane" : qUnion([Q0])});
            skLineSegment(sketch, "E75.0", {"start": v(54.1, 0) * mm, "end": v(54.1, -533.4) * mm, "construction": true});
            skLineSegment(sketch, "E76.0", {"start": v(-133.35, 0) * mm, "end": v(-133.35, -533.4) * mm, "construction": true});
            skLineSegment(sketch, "E77", {"start": v(-133.35, -266.7) * mm, "end": v(-250.55, -266.7) * mm, "construction": true});
            skLineSegment(sketch, "E78.0", {"start": v(-133.35, -482.6) * mm, "end": v(-250.55, -482.6) * mm, "construction": true});
            skPoint(sketch, "E79", {"position": v(-133.35, -482.6) * mm});
            skPoint(sketch, "E80", {"position": v(-133.35, -266.7) * mm});
            skPoint(sketch, "E81.MirrorP", {"position": v(-133.35, -50.8) * mm});
            skSolve(sketch);
        }
        {
            var Q0;
            Q0=sQuery(id+"F25.wireOp",VERTEX,"E79");
            var Q1;
            Q1=sQuery(id+"F25.wireOp",VERTEX,"E80");
            var Q2;
            Q2=sQuery(id+"F25.wireOp",VERTEX,"E81.MirrorP");
            var Q3;
            Q3=makeQuery(id+"F1.opExtrude","SWEPT_BODY",BODY,{"disambiguationData":[OSD([sQuery(id+"F0.wireOp",EDGE,"E1.bottom"),sQuery(id+"F0.wireOp",EDGE,"E1.left"),sQuery(id+"F0.wireOp",EDGE,"E1.right"),sQuery(id+"F0.wireOp",EDGE,"E4.bottom"),sQuery(id+"F0.wireOp",EDGE,"E4.left"),sQuery(id+"F0.wireOp",EDGE,"E4.right"),sQuery(id+"F0.wireOp",EDGE,"E5.bottom"),sQuery(id+"F0.wireOp",EDGE,"E5.top"),sQuery(id+"F0.wireOp",EDGE,"E5.left"),sQuery(id+"F0.wireOp",EDGE,"E5.right"),sQuery(id+"F0.wireOp",EDGE,"E6.filletArc"),sQuery(id+"F0.wireOp",EDGE,"E7.filletArc"),sQuery(id+"F0.wireOp",EDGE,"E11"),sQuery(id+"F0.wireOp",EDGE,"E12"),sQuery(id+"F0.wireOp",EDGE,"E15.trimOffspring"),sQuery(id+"F0.wireOp",EDGE,"E16.trimOffspring")])]});
            hole(context, id + "F26", {"style" : HoleStyle.SIMPLE, "endStyle" : HoleEndStyle.THROUGH, "standardTappedOrClearance" : lookupTablePath({ "standard" : "ANSI", "engagement" : "75%", "pitch" : "8 tpi", "size" : "1", "type" : "Tapped" }), "standardBlindInLast" : lookupTablePath({ "standard" : "ANSI", "engagement" : "75%", "pitch" : "8 tpi", "size" : "1", "type" : "Tapped" }), "holeDiameter" : 22.22 * mm, "showTappedDepth" : true, "tappedDepth" : 41.27 * mm, "tapClearance" : 3, "startFromSketch" : true, "locations" : qUnion([Q0, Q1, Q2]), "scope" : qUnion([Q3]), "majorDiameter" : 25.4 * mm});
        }
        {
            var Q0;
            Q0=makeQuery(id+"F1.opExtrude","CAP_FACE",FACE,{"disambiguationData":[OSD([sQuery(id+"F0.wireOp",EDGE,"E1.bottom"),sQuery(id+"F0.wireOp",EDGE,"E1.left"),sQuery(id+"F0.wireOp",EDGE,"E1.right"),sQuery(id+"F0.wireOp",EDGE,"E4.bottom"),sQuery(id+"F0.wireOp",EDGE,"E4.left"),sQuery(id+"F0.wireOp",EDGE,"E4.right"),sQuery(id+"F0.wireOp",EDGE,"E5.bottom"),sQuery(id+"F0.wireOp",EDGE,"E5.top"),sQuery(id+"F0.wireOp",EDGE,"E5.left"),sQuery(id+"F0.wireOp",EDGE,"E5.right"),sQuery(id+"F0.wireOp",EDGE,"E6.filletArc"),sQuery(id+"F0.wireOp",EDGE,"E7.filletArc"),sQuery(id+"F0.wireOp",EDGE,"E11"),sQuery(id+"F0.wireOp",EDGE,"E12"),sQuery(id+"F0.wireOp",EDGE,"E15.trimOffspring"),sQuery(id+"F0.wireOp",EDGE,"E16.trimOffspring")])],"isStart":false});
            var sketch = newSketch(context, id + "F27", { "sketchPlane" : qUnion([Q0])});
            skCircle(sketch, "E82.0", {"center": v(203.2, 701.55) * mm, "radius": 63.5 * mm, "construction": true});
            skLineSegment(sketch, "E83", {"start": v(203.2, 701.55) * mm, "end": v(693.11, 701.55) * mm, "construction": true});
            skLineSegment(sketch, "E84.0", {"start": v(203.2, 504.7) * mm, "end": v(688.88, 504.7) * mm, "construction": true});
            skLineSegment(sketch, "E85.bottom", {"start": v(688.88, 504.7) * mm, "end": v(-225.52, 504.7) * mm});
            skLineSegment(sketch, "E85.top", {"start": v(688.88, 111) * mm, "end": v(-225.52, 111) * mm});
            skLineSegment(sketch, "E85.left", {"start": v(688.88, 504.7) * mm, "end": v(688.88, 111) * mm});
            skLineSegment(sketch, "E85.right", {"start": v(-225.52, 504.7) * mm, "end": v(-225.52, 111) * mm});
            skSolve(sketch);
        }
        {
            var Q0;
            {var subQ0=sQuery(id+"F27.wireOp",EDGE,"E85.right");Q0=makeQuery(id+"F27.imprint","IMPRINT",FACE,{"disambiguationData":[TD([[makeQuery(id+"F27.imprint","IMPRINT",EDGE,{"derivedFrom":subQ0}),1.0]])]});}
            var Q1;
            Q1=makeQuery(id+"F27.imprint","IMPRINT",FACE,{"disambiguationData":[TD([[makeQuery(id+"F27.imprint","IMPRINT",EDGE,{"derivedFrom":makeQuery(id+"F11.hole-0.boolean.opBoolean","COPY",EDGE,{"derivedFrom":makeQuery(id+"F11.hole-0.opRevolve","SWEPT_EDGE",EDGE,{"disambiguationData":[OSD([sQuery(id+"F11.hole-0.sketch.wireOp",EDGE,"core_line_2"),sQuery(id+"F11.hole-0.sketch.wireOp",EDGE,"core_line_3")])]})})}),-1.0]])]});
            var Q2;
            {var subQ0=sQuery(id+"F27.wireOp",EDGE,"E85.left");Q2=makeQuery(id+"F27.imprint","IMPRINT",FACE,{"disambiguationData":[TD([[makeQuery(id+"F27.imprint","IMPRINT",EDGE,{"derivedFrom":subQ0}),-1.0]])]});}
            extrude(context, id + "F28", {"entities" : qUnion([Q0, Q1, Q2]), "operationType" : NewBodyOperationType.REMOVE, "oppositeDirection" : true, "depth" : 3.05 * mm});
        }
        {
            var Q0;
            {var subQ0=sQuery(id+"F0.wireOp",EDGE,"E16.trimOffspring");var subQ1=sQuery(id+"F0.wireOp",EDGE,"E7.filletArc");var subQ2=sQuery(id+"F0.wireOp",EDGE,"E5.top");var subQ3=sQuery(id+"F0.wireOp",EDGE,"E6.filletArc");var subQ4=sQuery(id+"F0.wireOp",EDGE,"E5.left");var subQ5=sQuery(id+"F0.wireOp",EDGE,"E4.left");var subQ6=sQuery(id+"F0.wireOp",EDGE,"E1.left");var subQ7=sQuery(id+"F0.wireOp",EDGE,"E1.right");var subQ8=sQuery(id+"F0.wireOp",EDGE,"E4.right");var subQ9=sQuery(id+"F0.wireOp",EDGE,"E15.trimOffspring");var subQ10=sQuery(id+"F0.wireOp",EDGE,"E5.bottom");Q0=makeQuery(id+"F28.boolean.opBoolean","SPLIT",FACE,{"disambiguationData":[TD([makeQuery(id+"F1.opExtrude","SWEPT_FACE",FACE,{"disambiguationData":[OSD([subQ8])]})])],"derivedFrom":makeQuery(id+"F1.opExtrude","CAP_FACE",FACE,{"disambiguationData":[OSD([sQuery(id+"F0.wireOp",EDGE,"E1.bottom"),subQ6,subQ7,sQuery(id+"F0.wireOp",EDGE,"E4.bottom"),subQ5,subQ8,subQ10,subQ2,subQ4,sQuery(id+"F0.wireOp",EDGE,"E5.right"),subQ3,subQ1,sQuery(id+"F0.wireOp",EDGE,"E11"),sQuery(id+"F0.wireOp",EDGE,"E12"),subQ9,subQ0])],"isStart":false})});}
            cPlane(context, id + "F29", {"entities" : qUnion([Q0]), "cplaneType" : CPlaneType.OFFSET, "offset" : 304.8 * mm, "width" : 152.4 * mm, "height" : 152.4 * mm});
        }
        {
            var Q0;
            Q0=makeQuery(id+"F1.opExtrude","SWEPT_BODY",BODY,{"disambiguationData":[OSD([sQuery(id+"F0.wireOp",EDGE,"E1.bottom"),sQuery(id+"F0.wireOp",EDGE,"E1.left"),sQuery(id+"F0.wireOp",EDGE,"E1.right"),sQuery(id+"F0.wireOp",EDGE,"E4.bottom"),sQuery(id+"F0.wireOp",EDGE,"E4.left"),sQuery(id+"F0.wireOp",EDGE,"E4.right"),sQuery(id+"F0.wireOp",EDGE,"E5.bottom"),sQuery(id+"F0.wireOp",EDGE,"E5.top"),sQuery(id+"F0.wireOp",EDGE,"E5.left"),sQuery(id+"F0.wireOp",EDGE,"E5.right"),sQuery(id+"F0.wireOp",EDGE,"E6.filletArc"),sQuery(id+"F0.wireOp",EDGE,"E7.filletArc"),sQuery(id+"F0.wireOp",EDGE,"E11"),sQuery(id+"F0.wireOp",EDGE,"E12"),sQuery(id+"F0.wireOp",EDGE,"E15.trimOffspring"),sQuery(id+"F0.wireOp",EDGE,"E16.trimOffspring")])]});
            var Q1;
            Q1=qCreatedBy(id+"F29.planeOp",FACE);
            mirror(context, id + "F30", {"entities" : qUnion([Q0]), "mirrorPlane" : qUnion([Q1])});
        }
        {
            var Q0;
            Q0=makeQuery(id+"F1.opExtrude","SWEPT_BODY",BODY,{"disambiguationData":[OSD([sQuery(id+"F0.wireOp",EDGE,"E1.bottom"),sQuery(id+"F0.wireOp",EDGE,"E1.left"),sQuery(id+"F0.wireOp",EDGE,"E1.right"),sQuery(id+"F0.wireOp",EDGE,"E4.bottom"),sQuery(id+"F0.wireOp",EDGE,"E4.left"),sQuery(id+"F0.wireOp",EDGE,"E4.right"),sQuery(id+"F0.wireOp",EDGE,"E5.bottom"),sQuery(id+"F0.wireOp",EDGE,"E5.top"),sQuery(id+"F0.wireOp",EDGE,"E5.left"),sQuery(id+"F0.wireOp",EDGE,"E5.right"),sQuery(id+"F0.wireOp",EDGE,"E6.filletArc"),sQuery(id+"F0.wireOp",EDGE,"E7.filletArc"),sQuery(id+"F0.wireOp",EDGE,"E11"),sQuery(id+"F0.wireOp",EDGE,"E12"),sQuery(id+"F0.wireOp",EDGE,"E15.trimOffspring"),sQuery(id+"F0.wireOp",EDGE,"E16.trimOffspring")])]});
            deleteBodies(context, id + "F31", {"entities" : qUnion([Q0])});
        }
    });
